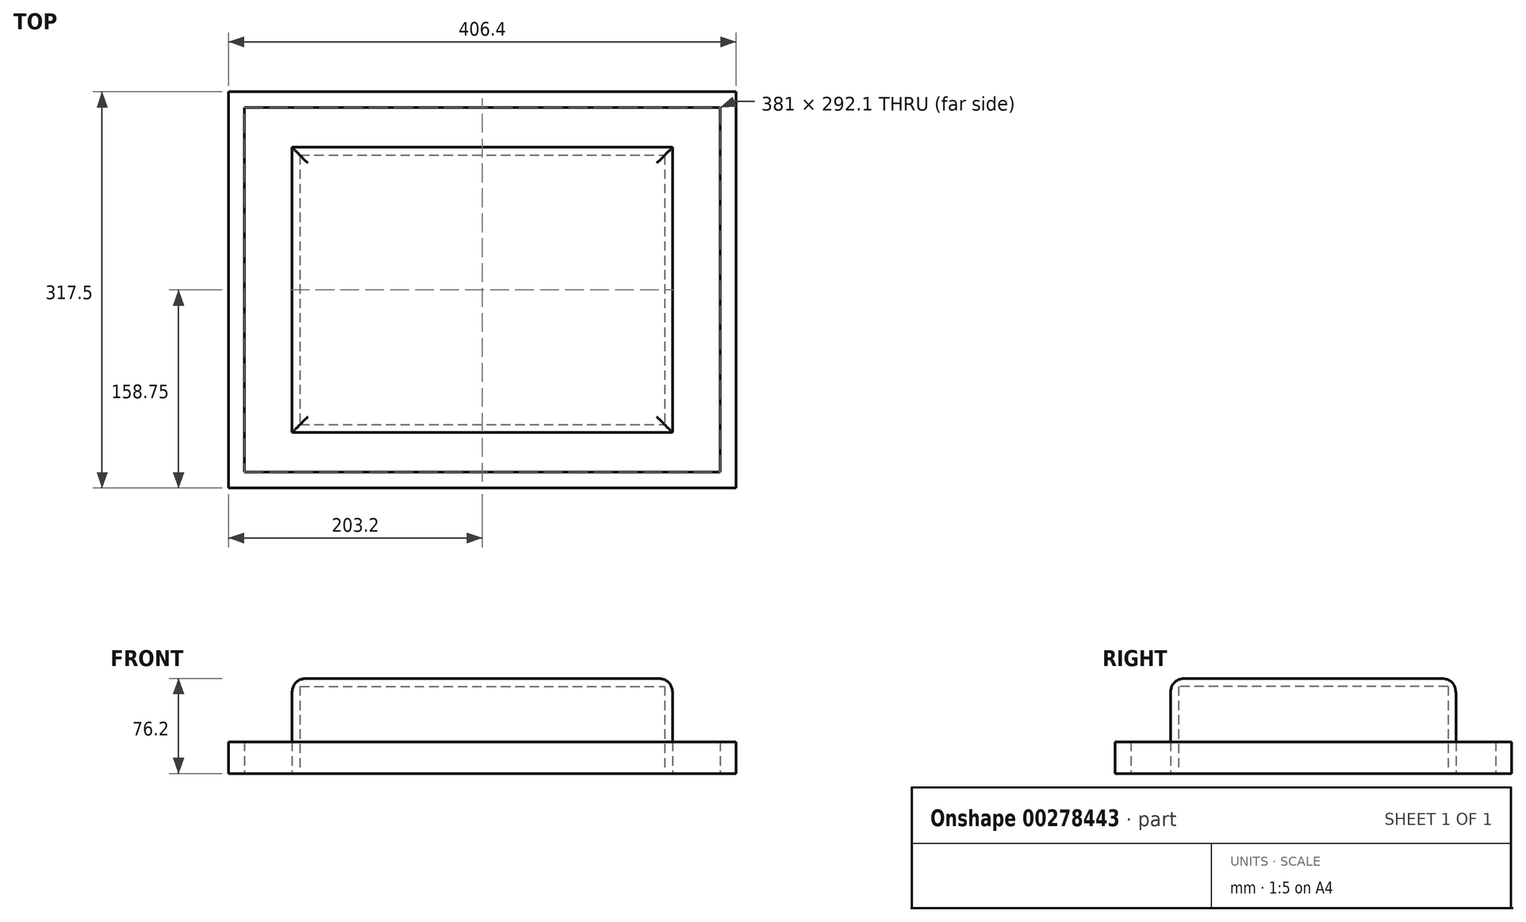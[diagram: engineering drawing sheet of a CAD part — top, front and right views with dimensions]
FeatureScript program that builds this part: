
annotation { "Feature Type Name" : "Feature", "Feature Type Description" : "" }
export const myFeature = defineFeature(function(context is Context, id is Id, definition is map)
    precondition{}
    {
        {
            var Q0;
            Q0=qCreatedBy(makeId("Top.planeOp"),FACE);
            var sketch = newSketch(context, id + "F0", { "sketchPlane" : qUnion([Q0])});
            skLineSegment(sketch, "E0.bottom", {"start": v(-152.4, 114.3) * mm, "end": v(152.4, 114.3) * mm});
            skLineSegment(sketch, "E0.top", {"start": v(-152.4, -114.3) * mm, "end": v(152.4, -114.3) * mm});
            skLineSegment(sketch, "E0.left", {"start": v(-152.4, 114.3) * mm, "end": v(-152.4, -114.3) * mm});
            skLineSegment(sketch, "E0.right", {"start": v(152.4, 114.3) * mm, "end": v(152.4, -114.3) * mm});
            skSolve(sketch);
        }
        {
            var Q0;
            Q0=makeQuery(id+"F0.imprint","IMPRINT",FACE,{"disambiguationData":[TD([[makeQuery(id+"F0.imprint","IMPRINT",EDGE,{"derivedFrom":sQuery(id+"F0.wireOp",EDGE,"E0.bottom")}),-1.0]])]});
            extrude(context, id + "F1", {"entities" : qUnion([Q0]), "depth" : 76.2 * mm});
        }
        {
            var Q0;
            Q0=makeQuery(id+"F1.opExtrude","CAP_FACE",FACE,{"disambiguationData":[OSD([sQuery(id+"F0.wireOp",EDGE,"E0.bottom"),sQuery(id+"F0.wireOp",EDGE,"E0.top"),sQuery(id+"F0.wireOp",EDGE,"E0.left"),sQuery(id+"F0.wireOp",EDGE,"E0.right")])],"isStart":true});
            shell(context, id + "F2", {"entities" : qUnion([Q0]), "thickness" : 6.35 * mm});
        }
        {
            var Q0;
            Q0=makeQuery(id+"F1.opExtrude","CAP_EDGE",EDGE,{"disambiguationData":[OSD([sQuery(id+"F0.wireOp",EDGE,"E0.top")])],"isStart":false});
            var Q1;
            Q1=makeQuery(id+"F1.opExtrude","CAP_EDGE",EDGE,{"disambiguationData":[OSD([sQuery(id+"F0.wireOp",EDGE,"E0.right")])],"isStart":false});
            var Q2;
            Q2=makeQuery(id+"F1.opExtrude","CAP_EDGE",EDGE,{"disambiguationData":[OSD([sQuery(id+"F0.wireOp",EDGE,"E0.bottom")])],"isStart":false});
            var Q3;
            Q3=makeQuery(id+"F1.opExtrude","CAP_EDGE",EDGE,{"disambiguationData":[OSD([sQuery(id+"F0.wireOp",EDGE,"E0.left")])],"isStart":false});
            fillet(context, id + "F3", {"entities" : qUnion([Q0, Q1, Q2, Q3]), "radius" : 12.7 * mm, "tangentPropagation" : true, "rho" : 0.5, "crossSection" : FilletCrossSection.CONIC, "allowEdgeOverflow" : false});
        }
        {
            var Q0;
            Q0=qCreatedBy(makeId("Top.planeOp"),FACE);
            var sketch = newSketch(context, id + "F4", { "sketchPlane" : qUnion([Q0])});
            skLineSegment(sketch, "E1.bottom", {"start": v(-203.2, -158.75) * mm, "end": v(203.2, -158.75) * mm});
            skLineSegment(sketch, "E1.top", {"start": v(-203.2, 158.75) * mm, "end": v(203.2, 158.75) * mm});
            skLineSegment(sketch, "E1.left", {"start": v(-203.2, -158.75) * mm, "end": v(-203.2, 158.75) * mm});
            skLineSegment(sketch, "E1.right", {"start": v(203.2, -158.75) * mm, "end": v(203.2, 158.75) * mm});
            skLineSegment(sketch, "E2.0", {"start": v(-190.5, -146.05) * mm, "end": v(-190.5, 146.05) * mm});
            skLineSegment(sketch, "E2.1", {"start": v(-190.5, -146.05) * mm, "end": v(190.5, -146.05) * mm});
            skLineSegment(sketch, "E2.2", {"start": v(190.5, -146.05) * mm, "end": v(190.5, 146.05) * mm});
            skLineSegment(sketch, "E2.3", {"start": v(-190.5, 146.05) * mm, "end": v(190.5, 146.05) * mm});
            skSolve(sketch);
        }
        {
            var Q0;
            Q0=makeQuery(id+"F4.imprint","IMPRINT",FACE,{"disambiguationData":[TD([[makeQuery(id+"F4.imprint","IMPRINT",EDGE,{"derivedFrom":sQuery(id+"F4.wireOp",EDGE,"E1.bottom")}),1.0]])]});
            extrude(context, id + "F5", {"entities" : qUnion([Q0]), "depth" : 25.4 * mm});
        }
    });
